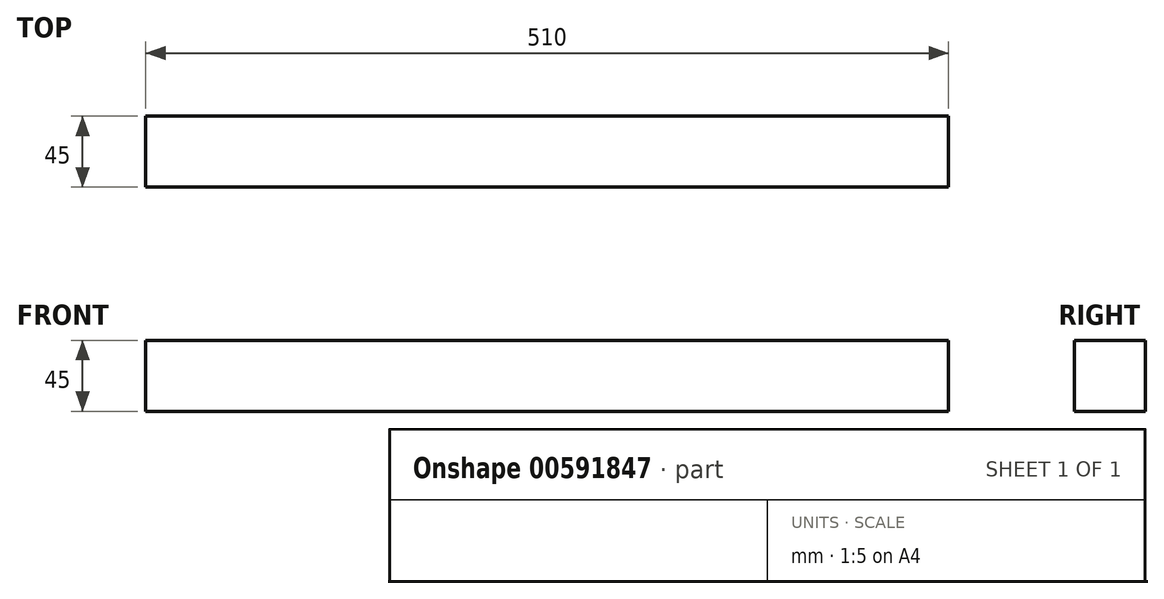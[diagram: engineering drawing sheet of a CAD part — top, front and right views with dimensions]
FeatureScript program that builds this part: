
annotation { "Feature Type Name" : "Feature", "Feature Type Description" : "" }
export const myFeature = defineFeature(function(context is Context, id is Id, definition is map)
    precondition{}
    {
        {
            var Q0;
            Q0=qCreatedBy(makeId("Right.planeOp"),FACE);
            var sketch = newSketch(context, id + "F0", { "sketchPlane" : qUnion([Q0])});
            skLineSegment(sketch, "E0.bottom", {"start": v(0, 0) * mm, "end": v(45, 0) * mm});
            skLineSegment(sketch, "E0.top", {"start": v(0, 45) * mm, "end": v(45, 45) * mm});
            skLineSegment(sketch, "E0.left", {"start": v(0, 0) * mm, "end": v(0, 45) * mm});
            skLineSegment(sketch, "E0.right", {"start": v(45, 0) * mm, "end": v(45, 45) * mm});
            skSolve(sketch);
        }
        {
            var Q0;
            Q0=makeQuery(id+"F0.imprint","IMPRINT",FACE,{"disambiguationData":[TD([[makeQuery(id+"F0.imprint","IMPRINT",EDGE,{"derivedFrom":sQuery(id+"F0.wireOp",EDGE,"E0.bottom")}),1.0]])]});
            extrude(context, id + "F1", {"entities" : qUnion([Q0]), "depth" : 510 * mm, "offsetDistance" : 25 * mm});
        }
    });
